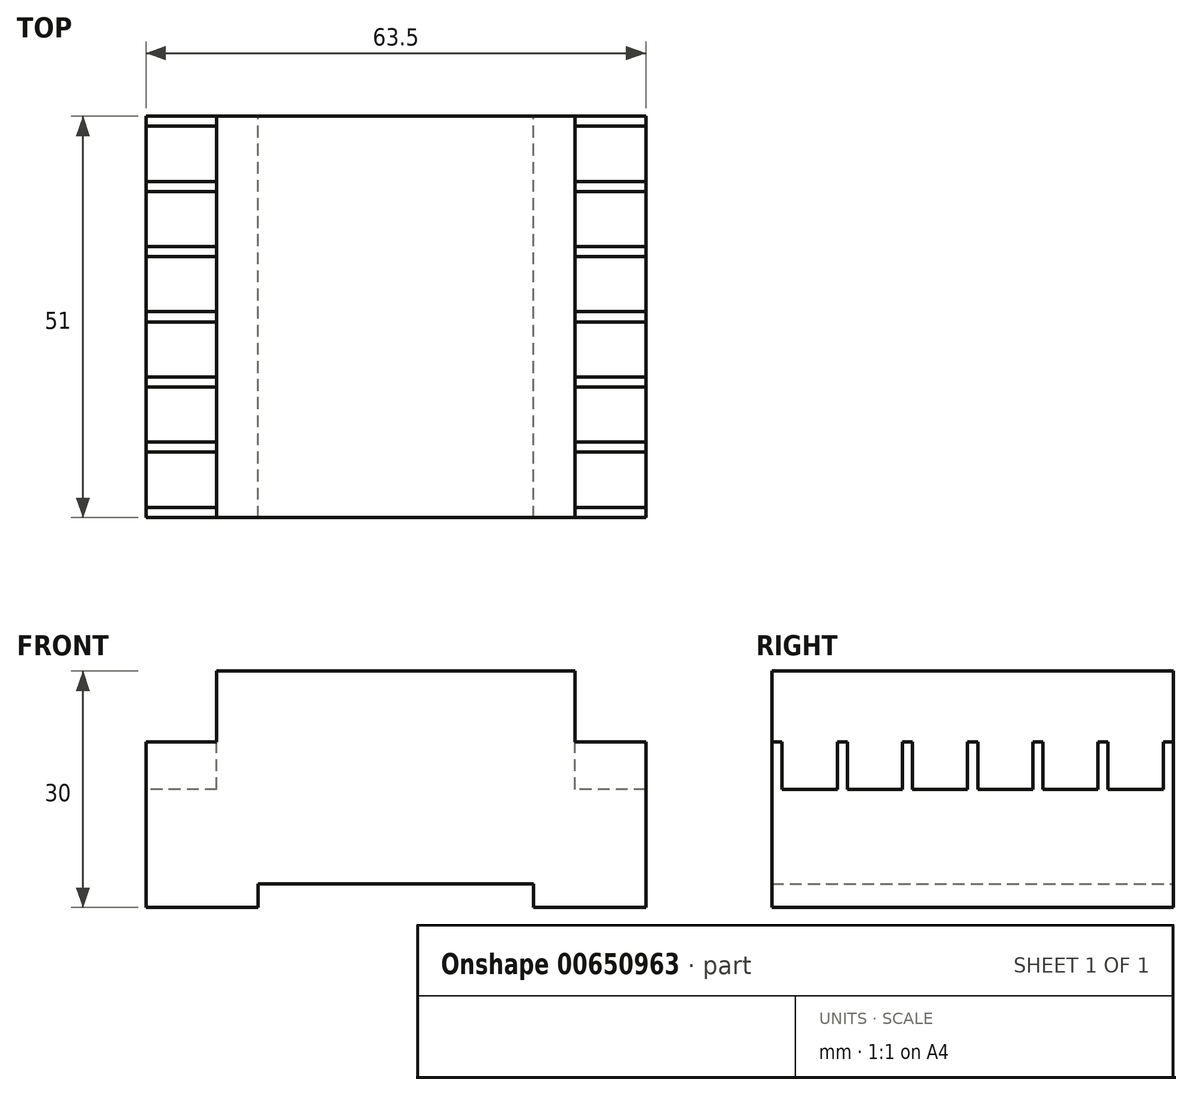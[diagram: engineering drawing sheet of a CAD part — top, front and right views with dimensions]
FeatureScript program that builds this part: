
annotation { "Feature Type Name" : "Feature", "Feature Type Description" : "" }
export const myFeature = defineFeature(function(context is Context, id is Id, definition is map)
    precondition{}
    {
        {
            var Q0;
            Q0=qCreatedBy(makeId("Front.planeOp"),FACE);
            var sketch = newSketch(context, id + "F0", { "sketchPlane" : qUnion([Q0])});
            skLineSegment(sketch, "E0.bottom", {"start": v(0, 0) * mm, "end": v(14.25, 0) * mm});
            skLineSegment(sketch, "E0.top", {"start": v(0, 21) * mm, "end": v(9, 21) * mm});
            skLineSegment(sketch, "E0.left", {"start": v(0, 0) * mm, "end": v(0, 21) * mm});
            skLineSegment(sketch, "E0.right", {"start": v(63.5, 0) * mm, "end": v(63.5, 21) * mm});
            skLineSegment(sketch, "E1.top", {"start": v(9, 30) * mm, "end": v(54.5, 30) * mm});
            skLineSegment(sketch, "E1.left", {"start": v(9, 21) * mm, "end": v(9, 30) * mm});
            skLineSegment(sketch, "E1.right", {"start": v(54.5, 21) * mm, "end": v(54.5, 30) * mm});
            skLineSegment(sketch, "E2.trimOffspring", {"start": v(54.5, 21) * mm, "end": v(63.5, 21) * mm});
            skLineSegment(sketch, "E3.top", {"start": v(14.25, 3) * mm, "end": v(49.25, 3) * mm});
            skLineSegment(sketch, "E3.left", {"start": v(14.25, 0) * mm, "end": v(14.25, 3) * mm});
            skLineSegment(sketch, "E3.right", {"start": v(49.25, 0) * mm, "end": v(49.25, 3) * mm});
            skLineSegment(sketch, "E4.trimOffspring", {"start": v(49.25, 0) * mm, "end": v(63.5, 0) * mm});
            skSolve(sketch);
        }
        {
            var Q0;
            Q0=makeQuery(id+"F0.imprint","IMPRINT",FACE,{"disambiguationData":[TD([[makeQuery(id+"F0.imprint","IMPRINT",EDGE,{"derivedFrom":sQuery(id+"F0.wireOp",EDGE,"E0.bottom")}),1.0]])]});
            extrude(context, id + "F1", {"entities" : qUnion([Q0]), "depth" : 51 * mm, "offsetDistance" : 25 * mm});
        }
        {
            var Q0;
            Q0=makeQuery(id+"F1.opExtrude","SWEPT_FACE",FACE,{"disambiguationData":[OSD([sQuery(id+"F0.wireOp",EDGE,"E2.trimOffspring")])]});
            var sketch = newSketch(context, id + "F2", { "sketchPlane" : qUnion([Q0])});
            skLineSegment(sketch, "E5.bottom", {"start": v(63.5, -1.28) * mm, "end": v(54.5, -1.28) * mm});
            skLineSegment(sketch, "E5.top", {"start": v(63.5, -8.28) * mm, "end": v(54.5, -8.28) * mm});
            skLineSegment(sketch, "E5.left", {"start": v(63.5, -1.28) * mm, "end": v(63.5, -8.28) * mm});
            skLineSegment(sketch, "E5.right", {"start": v(54.5, -1.28) * mm, "end": v(54.5, -8.28) * mm});
            skLineSegment(sketch, "E6.0.1.0", {"start": v(63.5, -16.56) * mm, "end": v(54.5, -16.56) * mm});
            skLineSegment(sketch, "E6.0.1.1", {"start": v(63.5, -9.56) * mm, "end": v(63.5, -16.56) * mm});
            skLineSegment(sketch, "E6.0.1.2", {"start": v(63.5, -9.56) * mm, "end": v(54.5, -9.56) * mm});
            skLineSegment(sketch, "E6.0.1.3", {"start": v(54.5, -9.56) * mm, "end": v(54.5, -16.56) * mm});
            skLineSegment(sketch, "E6.0.2.0", {"start": v(63.5, -24.84) * mm, "end": v(54.5, -24.84) * mm});
            skLineSegment(sketch, "E6.0.2.1", {"start": v(63.5, -17.84) * mm, "end": v(63.5, -24.84) * mm});
            skLineSegment(sketch, "E6.0.2.2", {"start": v(63.5, -17.84) * mm, "end": v(54.5, -17.84) * mm});
            skLineSegment(sketch, "E6.0.2.3", {"start": v(54.5, -17.84) * mm, "end": v(54.5, -24.84) * mm});
            skLineSegment(sketch, "E6.0.3.0", {"start": v(63.5, -33.12) * mm, "end": v(54.5, -33.12) * mm});
            skLineSegment(sketch, "E6.0.3.1", {"start": v(63.5, -26.12) * mm, "end": v(63.5, -33.12) * mm});
            skLineSegment(sketch, "E6.0.3.2", {"start": v(63.5, -26.12) * mm, "end": v(54.5, -26.12) * mm});
            skLineSegment(sketch, "E6.0.3.3", {"start": v(54.5, -26.12) * mm, "end": v(54.5, -33.12) * mm});
            skLineSegment(sketch, "E6.0.4.0", {"start": v(63.5, -41.4) * mm, "end": v(54.5, -41.4) * mm});
            skLineSegment(sketch, "E6.0.4.1", {"start": v(63.5, -34.4) * mm, "end": v(63.5, -41.4) * mm});
            skLineSegment(sketch, "E6.0.4.2", {"start": v(63.5, -34.4) * mm, "end": v(54.5, -34.4) * mm});
            skLineSegment(sketch, "E6.0.4.3", {"start": v(54.5, -34.4) * mm, "end": v(54.5, -41.4) * mm});
            skLineSegment(sketch, "E6.0.5.0", {"start": v(63.5, -49.68) * mm, "end": v(54.5, -49.68) * mm});
            skLineSegment(sketch, "E6.0.5.1", {"start": v(63.5, -42.68) * mm, "end": v(63.5, -49.68) * mm});
            skLineSegment(sketch, "E6.0.5.2", {"start": v(63.5, -42.68) * mm, "end": v(54.5, -42.68) * mm});
            skLineSegment(sketch, "E6.0.5.3", {"start": v(54.5, -42.68) * mm, "end": v(54.5, -49.68) * mm});
            skLineSegment(sketch, "E6.1.0.0", {"start": v(9, -8.28) * mm, "end": v(0, -8.28) * mm});
            skLineSegment(sketch, "E6.1.0.1", {"start": v(9, -1.28) * mm, "end": v(9, -8.28) * mm});
            skLineSegment(sketch, "E6.1.0.2", {"start": v(9, -1.28) * mm, "end": v(0, -1.28) * mm});
            skLineSegment(sketch, "E6.1.0.3", {"start": v(0, -1.28) * mm, "end": v(0, -8.28) * mm});
            skLineSegment(sketch, "E6.1.1.0", {"start": v(9, -16.56) * mm, "end": v(0, -16.56) * mm});
            skLineSegment(sketch, "E6.1.1.1", {"start": v(9, -9.56) * mm, "end": v(9, -16.56) * mm});
            skLineSegment(sketch, "E6.1.1.2", {"start": v(9, -9.56) * mm, "end": v(0, -9.56) * mm});
            skLineSegment(sketch, "E6.1.1.3", {"start": v(0, -9.56) * mm, "end": v(0, -16.56) * mm});
            skLineSegment(sketch, "E6.1.2.0", {"start": v(9, -24.84) * mm, "end": v(0, -24.84) * mm});
            skLineSegment(sketch, "E6.1.2.1", {"start": v(9, -17.84) * mm, "end": v(9, -24.84) * mm});
            skLineSegment(sketch, "E6.1.2.2", {"start": v(9, -17.84) * mm, "end": v(0, -17.84) * mm});
            skLineSegment(sketch, "E6.1.2.3", {"start": v(0, -17.84) * mm, "end": v(0, -24.84) * mm});
            skLineSegment(sketch, "E6.1.3.0", {"start": v(9, -33.12) * mm, "end": v(0, -33.12) * mm});
            skLineSegment(sketch, "E6.1.3.1", {"start": v(9, -26.12) * mm, "end": v(9, -33.12) * mm});
            skLineSegment(sketch, "E6.1.3.2", {"start": v(9, -26.12) * mm, "end": v(0, -26.12) * mm});
            skLineSegment(sketch, "E6.1.3.3", {"start": v(0, -26.12) * mm, "end": v(0, -33.12) * mm});
            skLineSegment(sketch, "E6.1.4.0", {"start": v(9, -41.4) * mm, "end": v(0, -41.4) * mm});
            skLineSegment(sketch, "E6.1.4.1", {"start": v(9, -34.4) * mm, "end": v(9, -41.4) * mm});
            skLineSegment(sketch, "E6.1.4.2", {"start": v(9, -34.4) * mm, "end": v(0, -34.4) * mm});
            skLineSegment(sketch, "E6.1.4.3", {"start": v(0, -34.4) * mm, "end": v(0, -41.4) * mm});
            skLineSegment(sketch, "E6.1.5.0", {"start": v(9, -49.68) * mm, "end": v(0, -49.68) * mm});
            skLineSegment(sketch, "E6.1.5.1", {"start": v(9, -42.68) * mm, "end": v(9, -49.68) * mm});
            skLineSegment(sketch, "E6.1.5.2", {"start": v(9, -42.68) * mm, "end": v(0, -42.68) * mm});
            skLineSegment(sketch, "E6.1.5.3", {"start": v(0, -42.68) * mm, "end": v(0, -49.68) * mm});
            skLineSegment(sketch, "E6.direction1", {"start": v(54.5, -8.28) * mm, "end": v(0, -8.28) * mm, "construction": true});
            skLineSegment(sketch, "E6.direction2", {"start": v(54.5, -8.28) * mm, "end": v(54.5, -16.56) * mm, "construction": true});
            skSolve(sketch);
        }
        {
            var Q0;
            Q0 = qSketchRegion(id + "F2", true);
            extrude(context, id + "F3", {"entities" : qUnion([Q0]), "operationType" : NewBodyOperationType.REMOVE, "oppositeDirection" : true, "depth" : 6 * mm, "offsetDistance" : 25 * mm});
        }
    });
